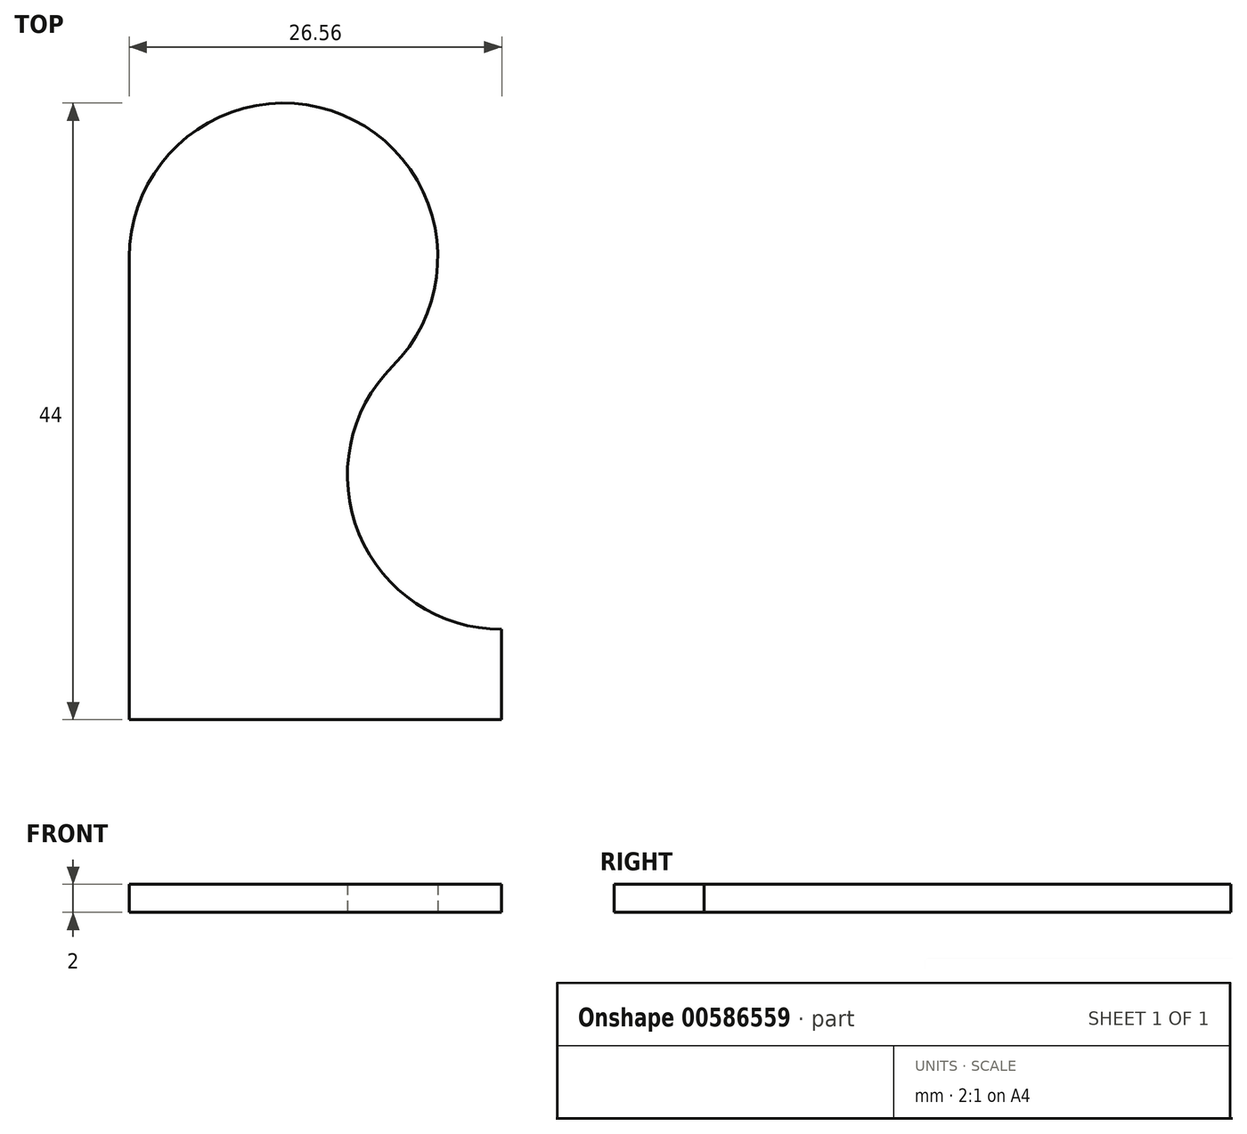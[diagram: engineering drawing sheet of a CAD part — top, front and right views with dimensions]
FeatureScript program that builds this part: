
annotation { "Feature Type Name" : "Feature", "Feature Type Description" : "" }
export const myFeature = defineFeature(function(context is Context, id is Id, definition is map)
    precondition{}
    {
        {
            var Q0;
            Q0=qCreatedBy(makeId("Top.planeOp"),FACE);
            var sketch = newSketch(context, id + "F0", { "sketchPlane" : qUnion([Q0])});
            skLineSegment(sketch, "E0", {"start": v(0, 0) * mm, "end": v(0, 33) * mm});
            skArc(sketch, "E1", {"start": v(0, 33) * mm, "mid": v(15.2, 43.16) * mm, "end": v(18.78, 25.22) * mm});
            skArc(sketch, "E2", {"start": v(18.78, 25.22) * mm, "mid": v(16.4, 13.23) * mm, "end": v(26.56, 6.44) * mm});
            skLineSegment(sketch, "E3", {"start": v(11, 33) * mm, "end": v(26.56, 17.44) * mm, "construction": true});
            skLineSegment(sketch, "E4", {"start": v(26.56, 0) * mm, "end": v(26.56, 17.44) * mm, "construction": true});
            skLineSegment(sketch, "E5", {"start": v(0, 0) * mm, "end": v(26.56, 0) * mm});
            skLineSegment(sketch, "E6", {"start": v(26.56, 6.44) * mm, "end": v(26.56, 0) * mm});
            skLineSegment(sketch, "E7", {"start": v(0, 33) * mm, "end": v(11, 33) * mm, "construction": true});
            skLineSegment(sketch, "E8", {"start": v(11, 33) * mm, "end": v(11, 22) * mm, "construction": true});
            skLineSegment(sketch, "E9", {"start": v(11, 22) * mm, "end": v(11, 11) * mm, "construction": true});
            skLineSegment(sketch, "E10", {"start": v(11, 0) * mm, "end": v(11, 11) * mm, "construction": true});
            skSolve(sketch);
        }
        {
            var Q0;
            Q0=qSketchRegion(id+"F0",true);
            extrude(context, id + "F1", {"entities" : qUnion([Q0]), "depth" : 2 * mm, "offsetDistance" : 25 * mm});
        }
    });
